# Revit family: HOSPIVAC V3 SIRELLA
name_source: partatom
category: Equipement de génie climatique
revit_build: Autodesk Revit 2018 (Build: 20170223_1515(x64)
units: mm (PartAtom-declared; Revit-internal decimal feet)

## family parameters
Basée sur le plan de construction = Non
Classification = Pompe
Cote de connecteur circulaire = Utiliser le diamètre
Couper avec des vides une fois chargée = Non
Partagée = Oui
Point de calcul de pièce = Non
Toujours verticalement = Oui
Type d'élément = Normal

## types (3) — shared parameters
COS_PHI = 0.9
DESCR_ALIM_X = Alimentation X ; 5G2.5mm²
DESCR_ALIM_Y = Alimentation Y ; 5G6mm²
DIAM_ASPI_VIDE = 50 mm  [stored 0.164042 ft]
DIAM_COLLECTEUR = 219.1 mm  [stored 0.718832 ft]
DIAM_EXT_ASPI = 56.7 mm
DIAM_REFOUL_VIDE = 50 mm  [stored 0.164042 ft]
DIST_TUY_REFOUL = 314 mm  [stored 1.03018 ft]
DOUBLE_ALIMENTATION = Oui
Ecartement UPA = 250 mm  [stored 0.82021 ft]
FREQUENCE = 50 Hz
Fabricant = MIL'S
HAUTEUR = 1885 mm
HAUT_ASPI = 1138 mm
HAUT_ASPI_1 = 887 mm
HAUT_ASPI_2 = 1767 mm
HAUT_OFFSET_COFFR = 100 mm  [stored 0.328084 ft]
HAUT_PLATEAU = 1100 mm
HAUT_PROCOM = 195 mm  [stored 0.639764 ft]
HT BOSSAGE 1 = 598 mm  [stored 1.96194 ft]
LARGEUR = 1120 mm
LARG_CHANFREIN_PLATEAU = 134 mm
LARG_COFFR = 300 mm
LARG_PLATEAU = 604 mm
LONGUEUR = 1325 mm
LONG_COFFR = 600 mm
LONG_DEPART_TUY_REFOUL = 314 mm  [stored 1.03018 ft]
LONG_IPA = 815 mm
LONG_PLATEAU_AR. = 254 mm
LONG_PLATEAU_AV. = 429 mm
LONG_PROCOM = 245 mm  [stored 0.803806 ft]
LONG_TUY_REFOUL = 563 mm  [stored 1.84711 ft]
Lien espace client = https://www.mils.fr
Modèle = HOSPIVAC V3 SIRELLA
NBR_POLES = 3
NEUTRE = Oui
OFFSET_UPA = 270 mm  [stored 0.885827 ft]
PLATEAU = 743 mm
POS_X_BOSSAGE_ASPI = 621 mm  [stored 2.0374 ft]
RAYON_ASPI_VIDE = 25 mm  [stored 0.082021 ft]
RAY_ALIM = 9.5 mm  [stored 0.031168 ft]
TENSION_ALIM = 400 V
TERRE = Oui
Zone de maintenance 1 = Non
Zone de maintenance coffret = Non
tab = GAZ
zero-valued in all types: 0

## per-type parameters (varying)
- HOSPIVAC V3 SL300.R: DEBIT_ASPI_VIDE=780.0 m³/h; DEBIT_REFOUL_VIDE=780.0 m³/h; DEGAG_CALORIFIQUE(kJ/h)=68215; DESCR_ASPI=Aspiration Vide 780m3/h ; G 2" FEM; DESCR_REFOUL=Refoulement Vide 780m3/h ; G 2" FEM; DESCR_RESERV=Vanne 2" pour départ réservoir; Ecartement pompes=791 mm; HAUT_BOSS3=64 mm  [stored 0.209974 ft]; HAUT_COFFR=285 mm; HAUT_OFFSET_FIX=24.5 mm; HAUT_REFOUL=302 mm; LARG_ECART_REFOUL=214 mm  [stored 0.7021 ft]; LARG_OFFSET_ALIM=34.9 mm; LARG_OFFSET_CONNECT_RESERV=197.6 mm; LARG_REFOUL_GAUCHE=575.5 mm; LARG_SORTIE_POMPE_G=575 mm; LONG_OFFSET_ALIM=250.2 mm; LONG_OFFSET_POMPE=802 mm; NIVEAU_SONORE(dB(A))=70; POIDS(Kg)=1070 mm; PROTEC_ELECT_X=Disjoncteur courbe D - 16 A; PROTEC_ELECT_Y=Disjoncteur courbe D - 32 A; PUISS_APPARENTE_X=6111 VA; PUISS_APPARENTE_Y=12222 VA; PUISS_ELECT_X=5.5 kW; PUISS_ELECT_Y=11 kW; TAILLE_POMPE=SIRELLA SLR : SL300.R
- HOSPIVAC V3 SL150.R: DEBIT_ASPI_VIDE=420.0 m³/h; DEBIT_REFOUL_VIDE=420.0 m³/h; DEGAG_CALORIFIQUE(kJ/h)=37208; DESCR_ASPI=Aspiration Vide ; 420m3/h ; G 2" FEM; DESCR_REFOUL=Refoulement Vide ; 420m3/h ; G 2" FEM; DESCR_RESERV=Vanne 1"1/2 pour départ réservoir; Ecartement pompes=790 mm; HAUT_BOSS3=48.8 mm; HAUT_COFFR=300 mm; HAUT_OFFSET_FIX=15 mm  [stored 0.0492126 ft]; HAUT_REFOUL=287 mm  [stored 0.941601 ft]; LARG_ECART_REFOUL=240 mm  [stored 0.787402 ft]; LARG_OFFSET_ALIM=130 mm  [stored 0.426509 ft]; LARG_OFFSET_CONNECT_RESERV=150 mm; LARG_REFOUL_GAUCHE=550 mm; LARG_SORTIE_POMPE_G=550.5 mm; LONG_OFFSET_ALIM=263 mm  [stored 0.862861 ft]; LONG_OFFSET_POMPE=766 mm; NIVEAU_SONORE(dB(A))=69; POIDS(Kg)=740 mm; PROTEC_ELECT_X=Disjoncteur courbe D - 10 A; PROTEC_ELECT_Y=Disjoncteur courbe D - 16 A; PUISS_APPARENTE_X=3333 VA; PUISS_APPARENTE_Y=6667 VA; PUISS_ELECT_X=3 kW; PUISS_ELECT_Y=6 kW; TAILLE_POMPE=SIRELLA SLR : SL150.R
- HOSPIVAC V3 SL100.R: DEBIT_ASPI_VIDE=270.0 m³/h; DEBIT_REFOUL_VIDE=270.0 m³/h; DEGAG_CALORIFIQUE(kJ/h)=27286; DESCR_ASPI=Aspiration Vide ; 270 m3/h ; G 2" FEM; DESCR_REFOUL=Refoulement Vide ; 270 m3/h ; G 2" FEM; DESCR_RESERV=Vanne 1"1/2 pour départ réservoir; Ecartement pompes=790 mm; HAUT_BOSS3=48.8 mm; HAUT_COFFR=300 mm; HAUT_OFFSET_FIX=15 mm  [stored 0.0492126 ft]; HAUT_REFOUL=302 mm; LARG_ECART_REFOUL=240 mm  [stored 0.787402 ft]; LARG_OFFSET_ALIM=34.9 mm; LARG_OFFSET_CONNECT_RESERV=150 mm; LARG_REFOUL_GAUCHE=550 mm; LARG_SORTIE_POMPE_G=550.5 mm; LONG_OFFSET_ALIM=250.2 mm; LONG_OFFSET_POMPE=766 mm; NIVEAU_SONORE(dB(A))=69; POIDS(Kg)=710 mm; PROTEC_ELECT_X=Disjoncteur courbe D - 10 A; PROTEC_ELECT_Y=Disjoncteur courbe D - 16 A; PUISS_APPARENTE_X=2444 VA; PUISS_APPARENTE_Y=4889 VA; PUISS_ELECT_X=2.2 kW; PUISS_ELECT_Y=4.4 kW; TAILLE_POMPE=SIRELLA SLR : SL100.R

note: [stored X ft] marks values corroborated as IEEE doubles in the binary element streams (Revit-internal decimal feet)
